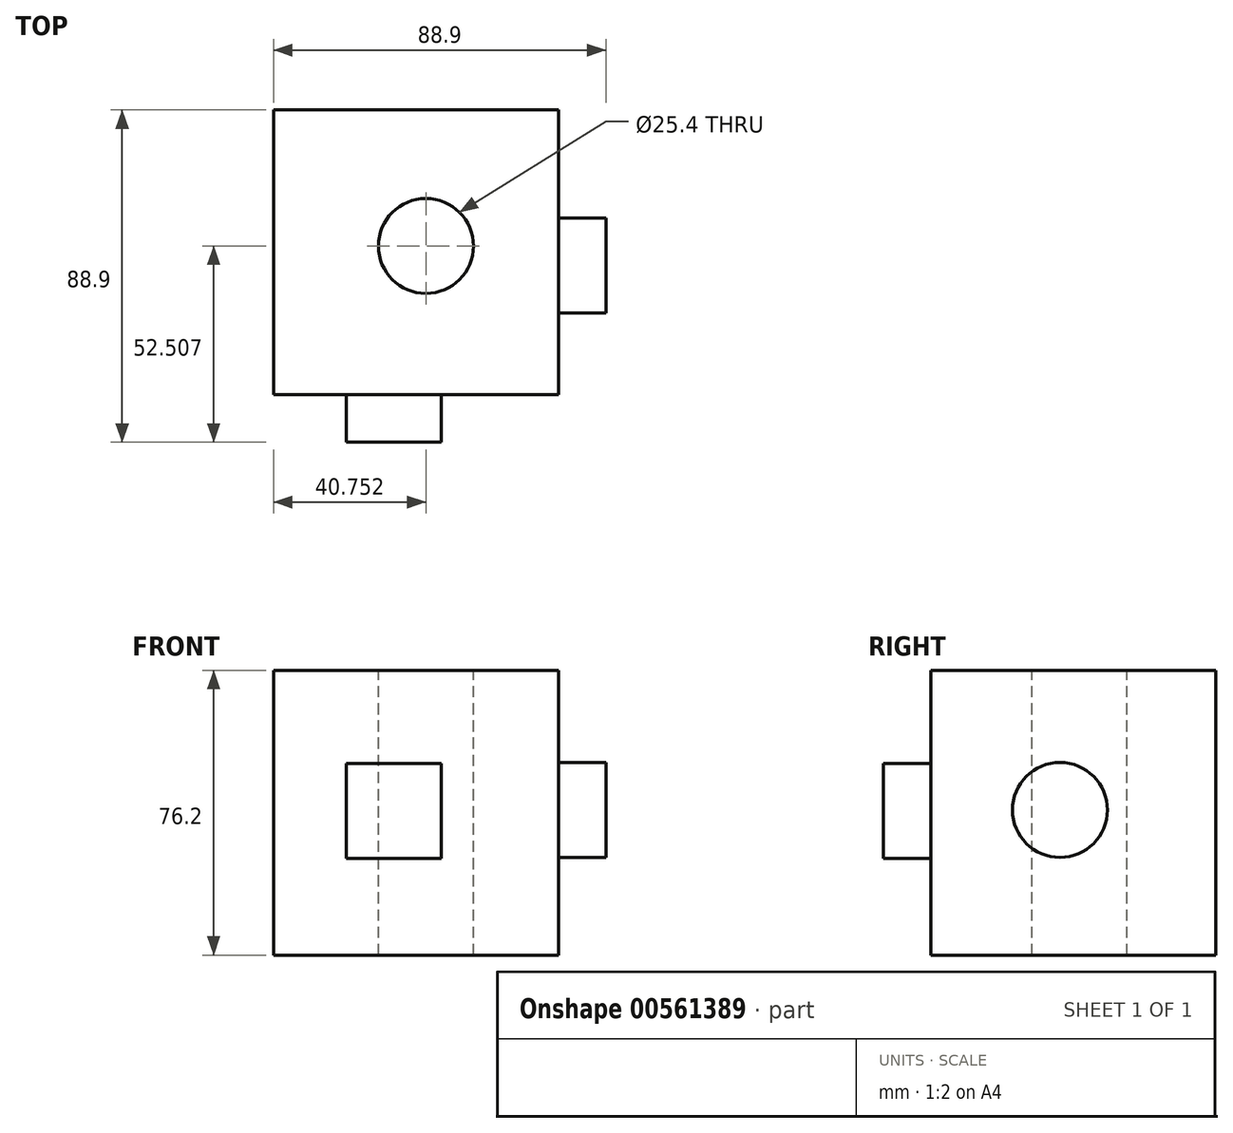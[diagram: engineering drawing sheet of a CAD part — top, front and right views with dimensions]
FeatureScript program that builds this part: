
annotation { "Feature Type Name" : "Feature", "Feature Type Description" : "" }
export const myFeature = defineFeature(function(context is Context, id is Id, definition is map)
    precondition{}
    {
        {
            var Q0;
            Q0=qCreatedBy(makeId("Front.planeOp"),FACE);
            var sketch = newSketch(context, id + "F0", { "sketchPlane" : qUnion([Q0])});
            skLineSegment(sketch, "E0.bottom", {"start": v(0, 0) * mm, "end": v(76.2, 0) * mm});
            skLineSegment(sketch, "E0.top", {"start": v(0, 76.2) * mm, "end": v(76.2, 76.2) * mm});
            skLineSegment(sketch, "E0.left", {"start": v(0, 0) * mm, "end": v(0, 76.2) * mm});
            skLineSegment(sketch, "E0.right", {"start": v(76.2, 0) * mm, "end": v(76.2, 76.2) * mm});
            skSolve(sketch);
        }
        {
            var Q0;
            Q0=makeQuery(id+"F0.imprint","IMPRINT",FACE,{"disambiguationData":[TD([[makeQuery(id+"F0.imprint","IMPRINT",EDGE,{"derivedFrom":sQuery(id+"F0.wireOp",EDGE,"E0.bottom")}),1.0]])]});
            extrude(context, id + "F1", {"entities" : qUnion([Q0]), "depth" : 76.2 * mm, "offsetDistance" : 25.4 * mm});
        }
        {
            var Q0;
            Q0=makeQuery(id+"F1.opExtrude","SWEPT_FACE",FACE,{"disambiguationData":[OSD([sQuery(id+"F0.wireOp",EDGE,"E0.top")])]});
            var sketch = newSketch(context, id + "F2", { "sketchPlane" : qUnion([Q0])});
            skCircle(sketch, "E1", {"center": v(40.75, -36.4) * mm, "radius": 12.7 * mm});
            skSolve(sketch);
        }
        {
            var Q0;
            Q0=sQuery(id+"F2.wireOp",VERTEX,"E1.center");
            var Q1;
            Q1=makeQuery(id+"F1.opExtrude","SWEPT_BODY",BODY,{"disambiguationData":[OSD([sQuery(id+"F0.wireOp",EDGE,"E0.bottom"),sQuery(id+"F0.wireOp",EDGE,"E0.top"),sQuery(id+"F0.wireOp",EDGE,"E0.left"),sQuery(id+"F0.wireOp",EDGE,"E0.right")])]});
            hole(context, id + "F3", {"style" : HoleStyle.SIMPLE, "endStyle" : HoleEndStyle.THROUGH, "holeDiameter" : 25.4 * mm, "isTappedThrough" : true, "tappedDepth" : 12.7 * mm, "tapClearance" : 3, "locations" : qUnion([Q0]), "scope" : qUnion([Q1])});
        }
        {
            var Q0;
            Q0=makeQuery(id+"F1.opExtrude","SWEPT_FACE",FACE,{"disambiguationData":[OSD([sQuery(id+"F0.wireOp",EDGE,"E0.right")])]});
            var sketch = newSketch(context, id + "F4", { "sketchPlane" : qUnion([Q0])});
            skCircle(sketch, "E2", {"center": v(-41.67, 38.83) * mm, "radius": 12.7 * mm});
            skSolve(sketch);
        }
        {
            var Q0;
            Q0 = qSketchRegion(id + "F4", true);
            extrude(context, id + "F5", {"entities" : qUnion([Q0]), "operationType" : NewBodyOperationType.ADD, "depth" : 12.7 * mm, "offsetDistance" : 25.4 * mm});
        }
        {
            var Q0;
            Q0=makeQuery(id+"F1.opExtrude","CAP_FACE",FACE,{"disambiguationData":[OSD([sQuery(id+"F0.wireOp",EDGE,"E0.bottom"),sQuery(id+"F0.wireOp",EDGE,"E0.top"),sQuery(id+"F0.wireOp",EDGE,"E0.left"),sQuery(id+"F0.wireOp",EDGE,"E0.right")])],"isStart":false});
            var sketch = newSketch(context, id + "F6", { "sketchPlane" : qUnion([Q0])});
            skLineSegment(sketch, "E3.bottom", {"start": v(19.52, 51.2) * mm, "end": v(44.92, 51.2) * mm});
            skLineSegment(sketch, "E3.top", {"start": v(19.52, 25.8) * mm, "end": v(44.92, 25.8) * mm});
            skLineSegment(sketch, "E3.left", {"start": v(19.52, 51.2) * mm, "end": v(19.52, 25.8) * mm});
            skLineSegment(sketch, "E3.right", {"start": v(44.92, 51.2) * mm, "end": v(44.92, 25.8) * mm});
            skSolve(sketch);
        }
        {
            var Q0;
            Q0 = qSketchRegion(id + "F6", true);
            extrude(context, id + "F7", {"entities" : qUnion([Q0]), "operationType" : NewBodyOperationType.ADD, "depth" : 12.7 * mm, "offsetDistance" : 25.4 * mm});
        }
    });
